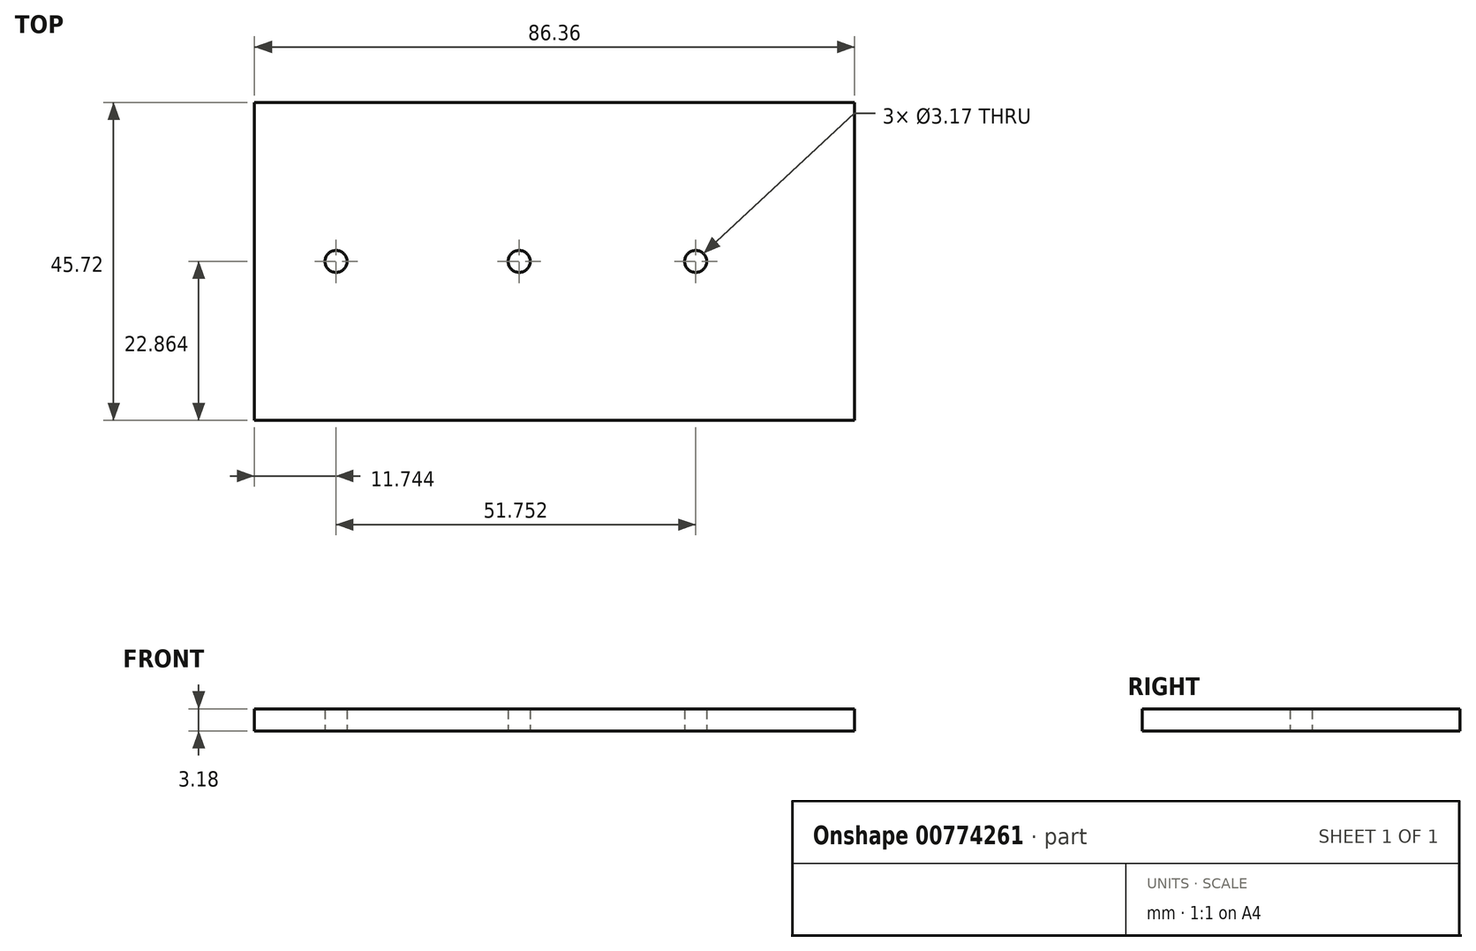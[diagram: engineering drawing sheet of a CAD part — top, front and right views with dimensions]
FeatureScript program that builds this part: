
annotation { "Feature Type Name" : "Feature", "Feature Type Description" : "" }
export const myFeature = defineFeature(function(context is Context, id is Id, definition is map)
    precondition{}
    {
        {
            var Q0;
            Q0=qCreatedBy(makeId("Top.planeOp"),FACE);
            var sketch = newSketch(context, id + "F0", { "sketchPlane" : qUnion([Q0])});
            skLineSegment(sketch, "E0.bottom", {"start": v(-38.86, 14.74) * mm, "end": v(39.88, 14.74) * mm, "construction": true});
            skLineSegment(sketch, "E0.top", {"start": v(-38.86, -23.36) * mm, "end": v(39.88, -23.36) * mm, "construction": true});
            skLineSegment(sketch, "E0.left", {"start": v(-38.86, 14.74) * mm, "end": v(-38.86, -23.36) * mm, "construction": true});
            skLineSegment(sketch, "E0.right", {"start": v(39.88, 14.74) * mm, "end": v(39.88, -23.36) * mm, "construction": true});
            skLineSegment(sketch, "E1.0", {"start": v(-42.67, 18.55) * mm, "end": v(43.69, 18.55) * mm});
            skLineSegment(sketch, "E1.1", {"start": v(-42.67, 18.55) * mm, "end": v(-42.67, -27.17) * mm});
            skLineSegment(sketch, "E1.2", {"start": v(-42.67, -27.17) * mm, "end": v(43.69, -27.17) * mm});
            skLineSegment(sketch, "E1.3", {"start": v(43.69, 18.55) * mm, "end": v(43.69, -27.17) * mm});
            skPoint(sketch, "E2", {"position": v(20.83, -4.3) * mm});
            skPoint(sketch, "E3", {"position": v(-4.57, -4.3) * mm});
            skPoint(sketch, "E4", {"position": v(-30.93, -4.3) * mm});
            skCircle(sketch, "E5", {"center": v(20.83, -4.3) * mm, "radius": 19.05 * mm, "construction": true});
            skCircle(sketch, "E6", {"center": v(-4.57, -4.3) * mm, "radius": 6.35 * mm, "construction": true});
            skCircle(sketch, "E7", {"center": v(-30.93, -4.3) * mm, "radius": 7.94 * mm, "construction": true});
            skCircle(sketch, "E8", {"center": v(-4.57, -4.3) * mm, "radius": 18.41 * mm, "construction": true});
            skCircle(sketch, "E9", {"center": v(-30.93, -4.3) * mm, "radius": 1.59 * mm});
            skCircle(sketch, "E10", {"center": v(-4.57, -4.3) * mm, "radius": 1.59 * mm});
            skCircle(sketch, "E11", {"center": v(20.83, -4.3) * mm, "radius": 1.59 * mm});
            skSolve(sketch);
        }
        {
            var Q0;
            Q0=makeQuery(id+"F0.imprint","IMPRINT",FACE,{"disambiguationData":[TD([[makeQuery(id+"F0.imprint","IMPRINT",EDGE,{"derivedFrom":sQuery(id+"F0.wireOp",EDGE,"E1.0")}),-1.0]])]});
            extrude(context, id + "F1", {"entities" : qUnion([Q0]), "depth" : 3.17 * mm, "offsetDistance" : 25.4 * mm});
        }
    });
